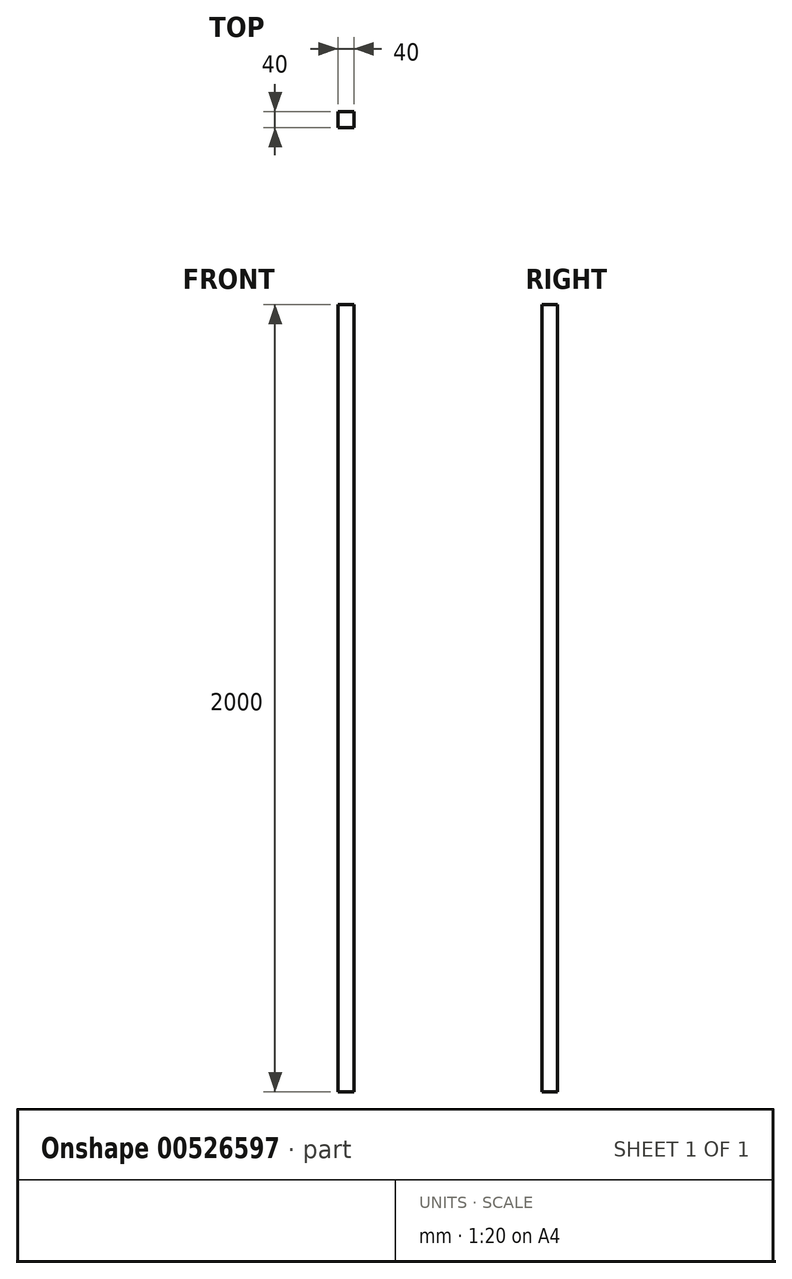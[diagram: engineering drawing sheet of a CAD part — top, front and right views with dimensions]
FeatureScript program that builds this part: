
annotation { "Feature Type Name" : "Feature", "Feature Type Description" : "" }
export const myFeature = defineFeature(function(context is Context, id is Id, definition is map)
    precondition{}
    {
        {
            var Q0;
            Q0=qCreatedBy(makeId("Top.planeOp"),FACE);
            var sketch = newSketch(context, id + "F0", { "sketchPlane" : qUnion([Q0])});
            skLineSegment(sketch, "E0.bottom", {"start": v(-72.4, -36.92) * mm, "end": v(-32.4, -36.92) * mm});
            skLineSegment(sketch, "E0.top", {"start": v(-72.4, 3.08) * mm, "end": v(-32.4, 3.08) * mm});
            skLineSegment(sketch, "E0.left", {"start": v(-72.4, -36.92) * mm, "end": v(-72.4, 3.08) * mm});
            skLineSegment(sketch, "E0.right", {"start": v(-32.4, -36.92) * mm, "end": v(-32.4, 3.08) * mm});
            skSolve(sketch);
        }
        {
            var Q0;
            Q0 = qSketchRegion(id + "F0", true);
            extrude(context, id + "F1", {"entities" : qUnion([Q0]), "depth" : 2000 * mm, "offsetDistance" : 25 * mm});
        }
    });
